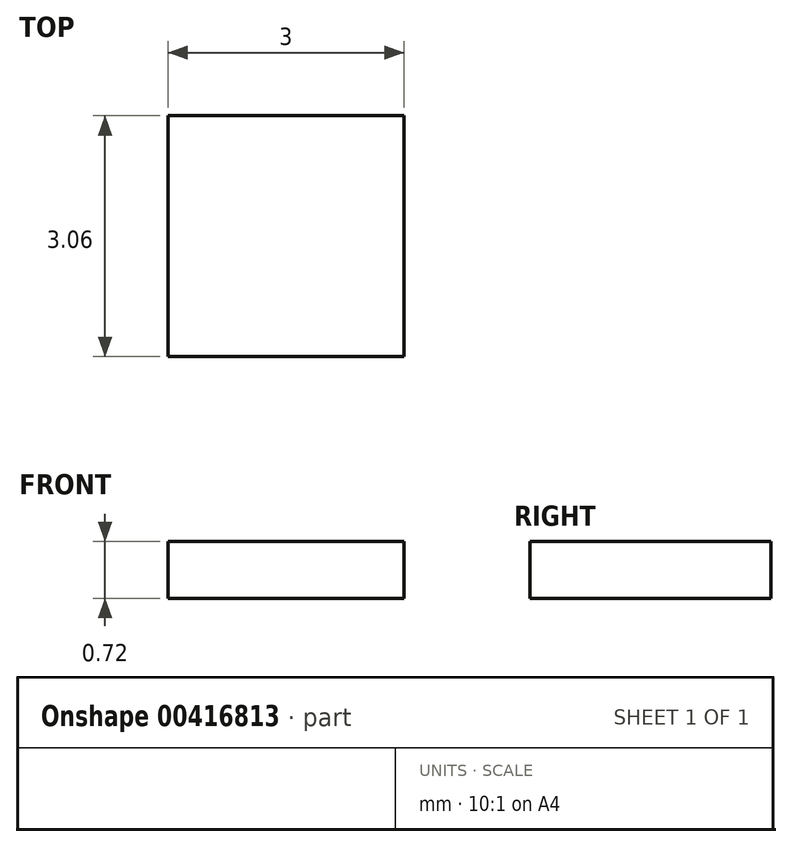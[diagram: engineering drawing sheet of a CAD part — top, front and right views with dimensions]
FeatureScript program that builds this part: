
annotation { "Feature Type Name" : "Feature", "Feature Type Description" : "" }
export const myFeature = defineFeature(function(context is Context, id is Id, definition is map)
    precondition{}
    {
        {
            var Q0;
            Q0=qCreatedBy(makeId("Top.planeOp"),FACE);
            var sketch = newSketch(context, id + "F0", { "sketchPlane" : qUnion([Q0])});
            skLineSegment(sketch, "E0.bottom", {"start": v(0, 0) * mm, "end": v(3, 0) * mm});
            skLineSegment(sketch, "E0.top", {"start": v(0, 3.06) * mm, "end": v(3, 3.06) * mm});
            skLineSegment(sketch, "E0.left", {"start": v(0, 0) * mm, "end": v(0, 3.06) * mm});
            skLineSegment(sketch, "E0.right", {"start": v(3, 0) * mm, "end": v(3, 3.06) * mm});
            skSolve(sketch);
        }
        {
            var Q0;
            Q0 = qSketchRegion(id + "F0", true);
            extrude(context, id + "F1", {"entities" : qUnion([Q0]), "depth" : .72 * mm, "offsetDistance" : 25.4 * mm});
        }
    });
